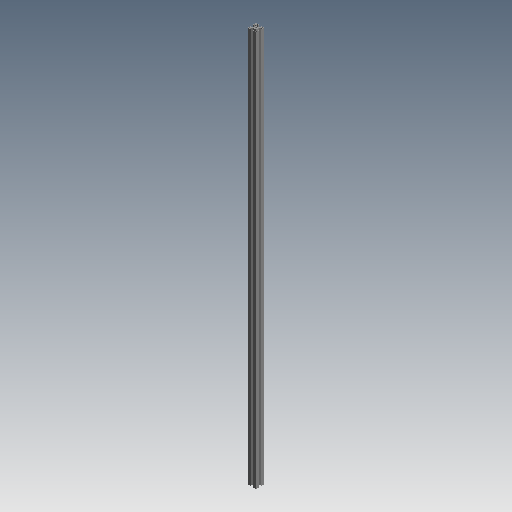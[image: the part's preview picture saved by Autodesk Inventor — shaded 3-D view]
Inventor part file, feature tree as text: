
AUTODESK INVENTOR PART (.ipt)
format: ipt  version: 2020 (Build 240168000, 168)  size: 211,968 bytes
history: native  units: mm (DEFAULTED — no unit token found)
features: other x21, sketch x3, hole x2, extrude x1, pattern_linear x1
ambient origin geometry x8: Origin, YZ Plane, XZ Plane, XY Plane, X Axis, Y Axis, Z Axis, Center Point
bodies: Solid1 (feature_tree)
feature tree (28):
  extrude  "Extrusion1"  Depth=1440.0mm
  hole  "Hole1"  [1 undecoded]
  hole  "Hole2"  [1 undecoded]
  pattern_linear  "Rectangular Pattern1"  [2 undecoded]
  other  "C1_XY"
  other  "C1_YZ"
  other  "C1_ZX"
  other  "C1_X"
  other  "C1_Y"
  other  "C1_Z"
  other  "C1_Center"
  other  "to_frame_cap1_XY"
  other  "to_frame_cap1_YZ"
  other  "to_frame_cap1_ZX"
  other  "to_frame_cap1_X"
  other  "to_frame_cap1_Y"
  other  "to_frame_cap1_Z"
  other  "to_frame_cap1_Center"
  other  "to_frame_cap2_XY"
  other  "to_frame_cap2_YZ"
  other  "to_frame_cap2_ZX"
  other  "to_frame_cap2_X"
  other  "to_frame_cap2_Y"
  other  "to_frame_cap2_Z"
  other  "to_frame_cap2_Center"
  sketch  "Sketch_1"  dims[d0=1440.0mm d1=0.0mm]
  sketch  "Sketch2"  dims[d2=6.8mm d3=6.0mm d4=4.0mm d5=2.0mm d6=90.0deg d7=1440.0mm d8=0.0mm]
  sketch  "Sketch3"  dims[d9=4.2mm d10=6.0mm d11=4.0mm d12=2.0mm d13=90.0deg d14=1440.0mm d15=0.0mm d16=20.0mm d18=23.2mm d19=20.0mm d21=23.2mm d22=0.0mm d23=0.0mm d24=0.0mm]
note: 4 required parameter values undecoded (feature->parameter linkage not recoverable at this tier; creation-order binding heuristic only, values carry confidence <= 0.55)
